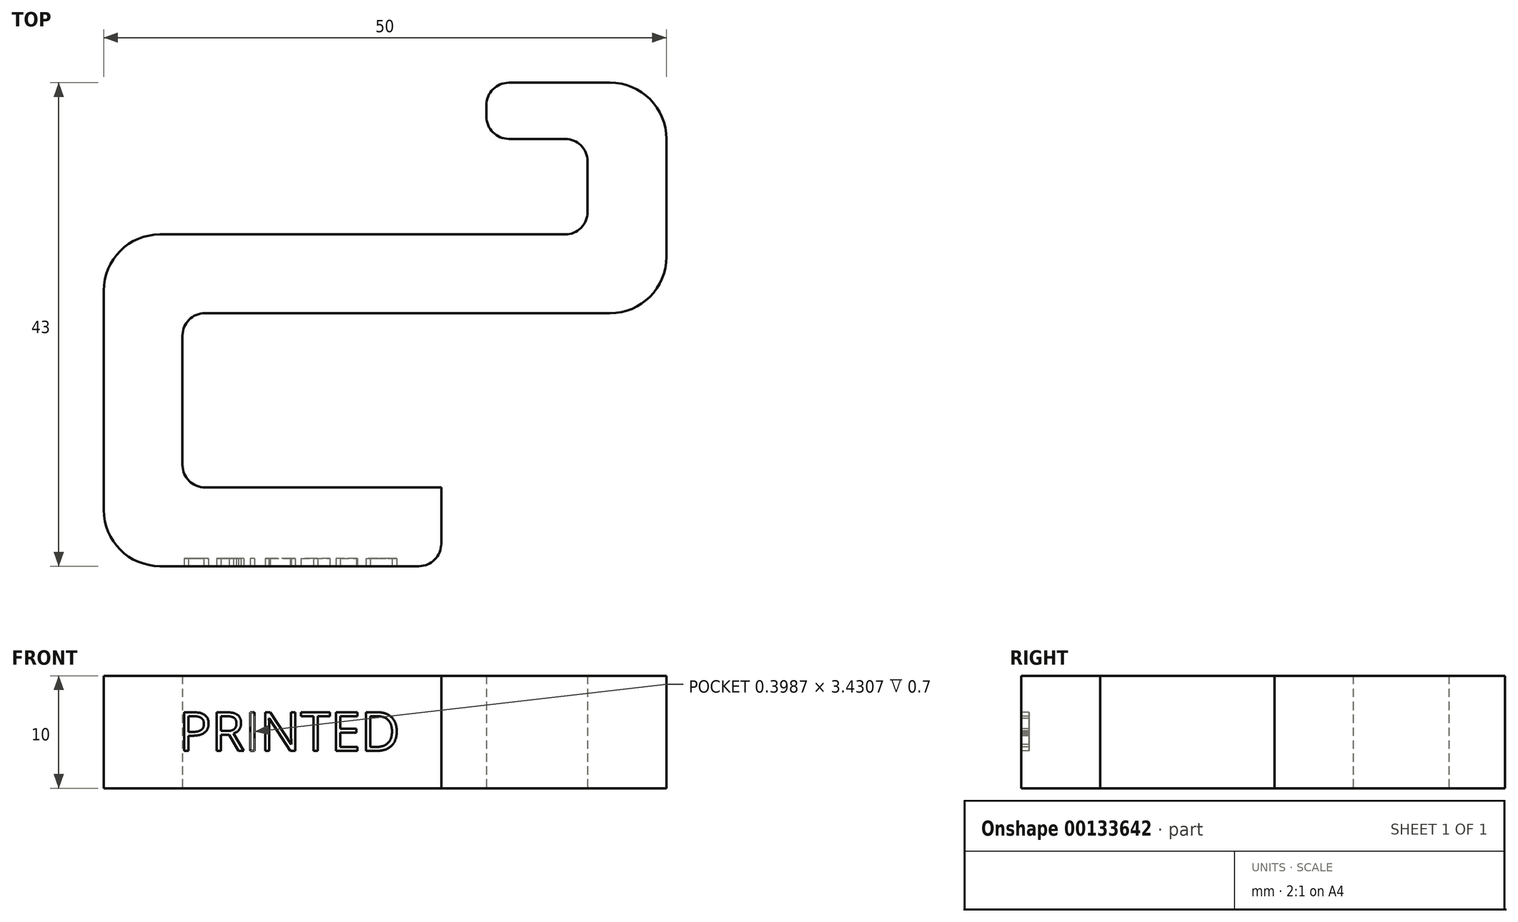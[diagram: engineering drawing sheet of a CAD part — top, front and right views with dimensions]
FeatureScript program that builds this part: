
annotation { "Feature Type Name" : "Feature", "Feature Type Description" : "" }
export const myFeature = defineFeature(function(context is Context, id is Id, definition is map)
    precondition{}
    {
        {
            var Q0;
            Q0=qCreatedBy(makeId("Top.planeOp"),FACE);
            var sketch = newSketch(context, id + "F0", { "sketchPlane" : qUnion([Q0])});
            skLineSegment(sketch, "E0.bottom", {"start": v(-30, 7) * mm, "end": v(20, 7) * mm});
            skLineSegment(sketch, "E0.top", {"start": v(-30, 0) * mm, "end": v(20, 0) * mm});
            skLineSegment(sketch, "E0.left", {"start": v(-30, 7) * mm, "end": v(-30, 0) * mm});
            skLineSegment(sketch, "E0.right", {"start": v(20, 7) * mm, "end": v(20, 0) * mm});
            skLineSegment(sketch, "E1.bottom", {"start": v(-30, 0) * mm, "end": v(-23, 0) * mm});
            skLineSegment(sketch, "E1.top", {"start": v(-30, -15.5) * mm, "end": v(-23, -15.5) * mm});
            skLineSegment(sketch, "E1.left", {"start": v(-30, 0) * mm, "end": v(-30, -15.5) * mm});
            skLineSegment(sketch, "E1.right", {"start": v(-23, 0) * mm, "end": v(-23, -15.5) * mm});
            skLineSegment(sketch, "E2.bottom", {"start": v(-30, -15.5) * mm, "end": v(0, -15.5) * mm});
            skLineSegment(sketch, "E2.top", {"start": v(-30, -22.5) * mm, "end": v(0, -22.5) * mm});
            skLineSegment(sketch, "E2.left", {"start": v(-30, -15.5) * mm, "end": v(-30, -22.5) * mm});
            skLineSegment(sketch, "E2.right", {"start": v(0, -15.5) * mm, "end": v(0, -22.5) * mm});
            skLineSegment(sketch, "E3.bottom", {"start": v(20, 7) * mm, "end": v(13, 7) * mm});
            skLineSegment(sketch, "E3.top", {"start": v(20, 15.5) * mm, "end": v(13, 15.5) * mm});
            skLineSegment(sketch, "E3.left", {"start": v(20, 7) * mm, "end": v(20, 15.5) * mm});
            skLineSegment(sketch, "E3.right", {"start": v(13, 7) * mm, "end": v(13, 15.5) * mm});
            skLineSegment(sketch, "E4.bottom", {"start": v(20, 15.5) * mm, "end": v(4, 15.5) * mm});
            skLineSegment(sketch, "E4.top", {"start": v(20, 20.5) * mm, "end": v(4, 20.5) * mm});
            skLineSegment(sketch, "E4.left", {"start": v(20, 15.5) * mm, "end": v(20, 20.5) * mm});
            skLineSegment(sketch, "E4.right", {"start": v(4, 15.5) * mm, "end": v(4, 20.5) * mm});
            skSolve(sketch);
        }
        {
            var Q0;
            Q0 = qSketchRegion(id + "F0", true);
            extrude(context, id + "F1", {"entities" : qUnion([Q0]), "depth" : 10 * mm});
        }
        {
            var Q0;
            Q0=makeQuery(id+"F1.opExtrude","SWEPT_EDGE",EDGE,{"disambiguationData":[OSD([sQuery(id+"F0.wireOp",EDGE,"E2.top"),sQuery(id+"F0.wireOp",EDGE,"E2.left")])]});
            var Q1;
            Q1=makeQuery(id+"F1.opExtrude","SWEPT_EDGE",EDGE,{"disambiguationData":[OSD([sQuery(id+"F0.wireOp",EDGE,"E0.bottom"),sQuery(id+"F0.wireOp",EDGE,"E0.left")])]});
            var Q2;
            Q2=makeQuery(id+"F1.opExtrude","SWEPT_EDGE",EDGE,{"disambiguationData":[OSD([sQuery(id+"F0.wireOp",EDGE,"E0.top"),sQuery(id+"F0.wireOp",EDGE,"E0.right")])]});
            var Q3;
            Q3=makeQuery(id+"F1.opExtrude","SWEPT_EDGE",EDGE,{"disambiguationData":[OSD([sQuery(id+"F0.wireOp",EDGE,"E4.top"),sQuery(id+"F0.wireOp",EDGE,"E4.left")])]});
            fillet(context, id + "F2", {"entities" : qUnion([Q0, Q1, Q2, Q3]), "radius" : 5 * mm, "tangentPropagation" : true, "allowEdgeOverflow" : false});
        }
        {
            var Q0;
            Q0=makeQuery(id+"F1.opExtrude","SWEPT_EDGE",EDGE,{"disambiguationData":[OSD([sQuery(id+"F0.wireOp",EDGE,"E0.top"),sQuery(id+"F0.wireOp",EDGE,"E1.bottom"),sQuery(id+"F0.wireOp",EDGE,"E1.right")])]});
            var Q1;
            Q1=makeQuery(id+"F1.opExtrude","SWEPT_EDGE",EDGE,{"disambiguationData":[OSD([sQuery(id+"F0.wireOp",EDGE,"E1.right"),sQuery(id+"F0.wireOp",EDGE,"E2.bottom")])]});
            var Q2;
            Q2=makeQuery(id+"F1.opExtrude","SWEPT_EDGE",EDGE,{"disambiguationData":[OSD([sQuery(id+"F0.wireOp",EDGE,"E2.top"),sQuery(id+"F0.wireOp",EDGE,"E2.right")])]});
            var Q3;
            Q3=makeQuery(id+"F1.opExtrude","SWEPT_EDGE",EDGE,{"disambiguationData":[OSD([sQuery(id+"F0.wireOp",EDGE,"E4.top"),sQuery(id+"F0.wireOp",EDGE,"E4.right")])]});
            var Q4;
            Q4=makeQuery(id+"F1.opExtrude","SWEPT_EDGE",EDGE,{"disambiguationData":[OSD([sQuery(id+"F0.wireOp",EDGE,"E4.bottom"),sQuery(id+"F0.wireOp",EDGE,"E4.right")])]});
            var Q5;
            Q5=makeQuery(id+"F1.opExtrude","SWEPT_EDGE",EDGE,{"disambiguationData":[OSD([sQuery(id+"F0.wireOp",EDGE,"E3.right"),sQuery(id+"F0.wireOp",EDGE,"E4.bottom")])]});
            var Q6;
            Q6=makeQuery(id+"F1.opExtrude","SWEPT_EDGE",EDGE,{"disambiguationData":[OSD([sQuery(id+"F0.wireOp",EDGE,"E0.bottom"),sQuery(id+"F0.wireOp",EDGE,"E3.bottom"),sQuery(id+"F0.wireOp",EDGE,"E3.right")])]});
            fillet(context, id + "F3", {"entities" : qUnion([Q0, Q1, Q2, Q3, Q4, Q5, Q6]), "radius" : 2 * mm, "tangentPropagation" : true, "allowEdgeOverflow" : false});
        }
        {
            var Q0;
            Q0=makeQuery(id+"F1.opExtrude","SWEPT_FACE",FACE,{"disambiguationData":[OSD([sQuery(id+"F0.wireOp",EDGE,"E2.top")])]});
            var sketch = newSketch(context, id + "F4", { "sketchPlane" : qUnion([Q0])});
            skText(sketch, "E5", { "text": "PRINTED", "fontName": "OpenSans-Regular.ttf"});
            const initialGuessF4  = {"E5": [-0.02333, 0.00332, 1, 0, 0.00346]};
            skSetInitialGuess(sketch, initialGuessF4);
            skSolve(sketch);
        }
        {
            var Q0;
            Q0 = qSketchRegion(id + "F4", true);
            extrude(context, id + "F5", {"entities" : qUnion([Q0]), "operationType" : NewBodyOperationType.REMOVE, "oppositeDirection" : true, "depth" : 0.7 * mm});
        }
    });
